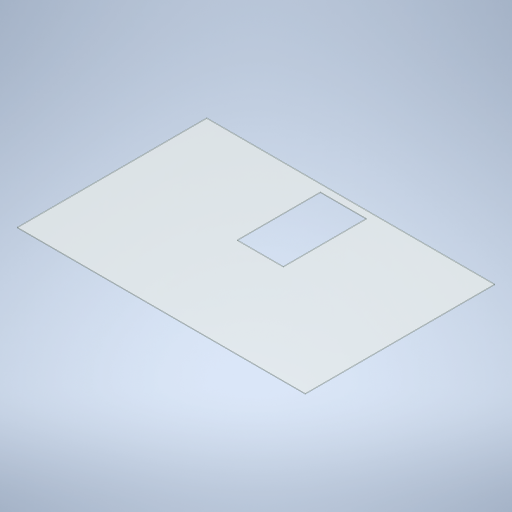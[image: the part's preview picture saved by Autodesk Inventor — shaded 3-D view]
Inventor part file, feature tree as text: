
AUTODESK INVENTOR PART (.ipt)
format: ipt  version: 2024 (Build 280153000, 153)  size: 241,152 bytes
history: native  units: in
note: dims shown in document units (in); Inventor stores cm internally (conversion verified against a paired STEP export)
features: extrude x2, sketch x2
ambient origin geometry x8: Origin, YZ Plane, XZ Plane, XY Plane, X Axis, Y Axis, Z Axis, Center Point
bodies: Solid1 (feature_tree)
feature tree (4):
  extrude  "Extrusion1"  Depth=291.5in
  extrude  "Extrusion2"  Depth=122.5in
  sketch  "Sketch1"  dims[d2=191.787in d3=291.5in]
  sketch  "Sketch2"  dims[d4=0.75in d5=0.0in d6=122.5in d7=7.5in d8=46.5in d9=84.0in d10=1.0in d11=0.0in]
